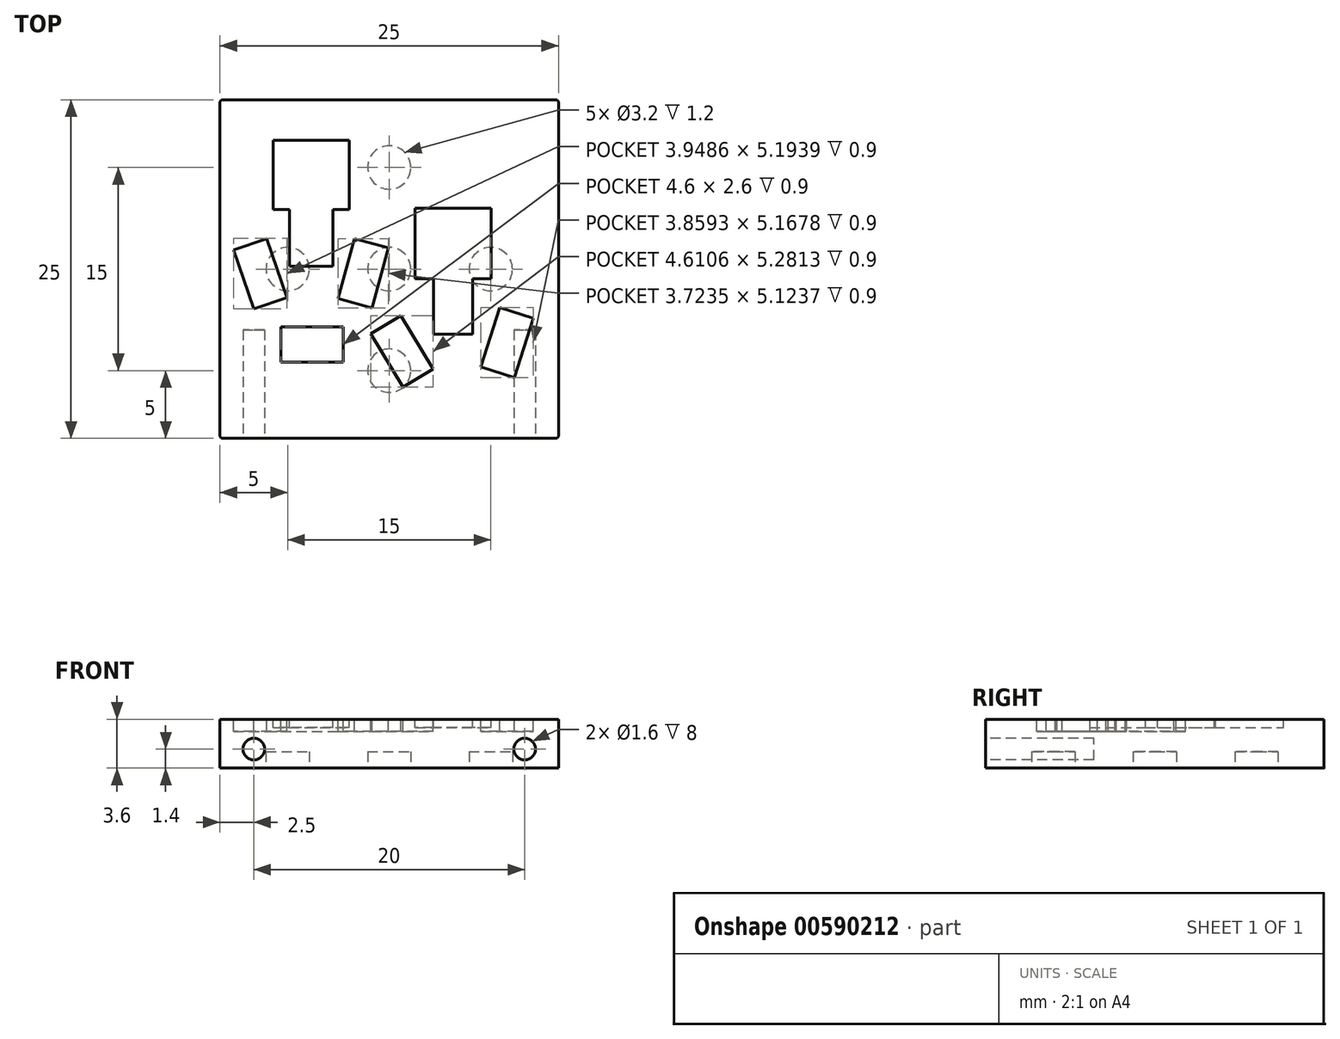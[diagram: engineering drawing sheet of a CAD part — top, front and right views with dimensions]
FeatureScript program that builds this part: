
annotation { "Feature Type Name" : "Feature", "Feature Type Description" : "" }
export const myFeature = defineFeature(function(context is Context, id is Id, definition is map)
    precondition{}
    {
        {
            var Q0;
            Q0=qCreatedBy(makeId("Top.planeOp"),FACE);
            var sketch = newSketch(context, id + "F0", { "sketchPlane" : qUnion([Q0])});
            skLineSegment(sketch, "E0.bottom", {"start": v(-12.5, 12.5) * mm, "end": v(12.5, 12.5) * mm});
            skLineSegment(sketch, "E0.top", {"start": v(-12.5, -12.5) * mm, "end": v(12.5, -12.5) * mm});
            skLineSegment(sketch, "E0.left", {"start": v(-12.5, 12.5) * mm, "end": v(-12.5, -12.5) * mm});
            skLineSegment(sketch, "E0.right", {"start": v(12.5, 12.5) * mm, "end": v(12.5, -12.5) * mm});
            skPoint(sketch, "E0.middle", {"position": v(0, 0) * mm});
            skSolve(sketch);
        }
        {
            var Q0;
            Q0 = qSketchRegion(id + "F0", true);
            extrude(context, id + "F1", {"entities" : qUnion([Q0]), "depth" : 3.6 * mm, "offsetDistance" : 25 * mm});
        }
        {
            var Q0;
            Q0=makeQuery(id+"F1.opExtrude","CAP_FACE",FACE,{"disambiguationData":[OSD([sQuery(id+"F0.wireOp",EDGE,"E0.bottom"),sQuery(id+"F0.wireOp",EDGE,"E0.top"),sQuery(id+"F0.wireOp",EDGE,"E0.left"),sQuery(id+"F0.wireOp",EDGE,"E0.right")])],"isStart":false});
            var sketch = newSketch(context, id + "F2", { "sketchPlane" : qUnion([Q0])});
            skLineSegment(sketch, "E1", {"start": v(-8.57, 9.5) * mm, "end": v(-2.97, 9.5) * mm});
            skLineSegment(sketch, "E2", {"start": v(-2.97, 9.5) * mm, "end": v(-2.97, 4.4) * mm});
            skLineSegment(sketch, "E3", {"start": v(-2.97, 4.4) * mm, "end": v(-4.17, 4.4) * mm});
            skLineSegment(sketch, "E4", {"start": v(-4.17, 4.4) * mm, "end": v(-4.17, 0.2) * mm});
            skLineSegment(sketch, "E5", {"start": v(-4.17, 0.2) * mm, "end": v(-7.37, 0.2) * mm});
            skLineSegment(sketch, "E6", {"start": v(-7.37, 0.2) * mm, "end": v(-7.37, 4.4) * mm});
            skLineSegment(sketch, "E7", {"start": v(-7.37, 4.4) * mm, "end": v(-8.57, 4.4) * mm});
            skLineSegment(sketch, "E8", {"start": v(-8.57, 4.4) * mm, "end": v(-8.57, 9.5) * mm});
            skLineSegment(sketch, "E9", {"start": v(1.91, 4.5) * mm, "end": v(7.51, 4.5) * mm});
            skLineSegment(sketch, "E10", {"start": v(7.51, 4.5) * mm, "end": v(7.51, -0.7) * mm});
            skLineSegment(sketch, "E11", {"start": v(7.51, -0.7) * mm, "end": v(6.16, -0.7) * mm});
            skLineSegment(sketch, "E12", {"start": v(6.16, -0.7) * mm, "end": v(6.16, -4.8) * mm});
            skLineSegment(sketch, "E13", {"start": v(6.16, -4.8) * mm, "end": v(3.26, -4.8) * mm});
            skLineSegment(sketch, "E14", {"start": v(3.26, -4.8) * mm, "end": v(3.26, -0.7) * mm});
            skLineSegment(sketch, "E15", {"start": v(3.26, -0.7) * mm, "end": v(1.91, -0.7) * mm});
            skLineSegment(sketch, "E16", {"start": v(1.91, -0.7) * mm, "end": v(1.91, 4.5) * mm});
            skSolve(sketch);
        }
        {
            var Q0;
            Q0 = qSketchRegion(id + "F2", true);
            extrude(context, id + "F3", {"entities" : qUnion([Q0]), "operationType" : NewBodyOperationType.REMOVE, "oppositeDirection" : true, "depth" : .6 * mm, "offsetDistance" : 25 * mm});
        }
        {
            var Q0;
            Q0=makeQuery(id+"F1.opExtrude","CAP_FACE",FACE,{"disambiguationData":[OSD([sQuery(id+"F0.wireOp",EDGE,"E0.bottom"),sQuery(id+"F0.wireOp",EDGE,"E0.top"),sQuery(id+"F0.wireOp",EDGE,"E0.left"),sQuery(id+"F0.wireOp",EDGE,"E0.right")])],"isStart":false});
            var sketch = newSketch(context, id + "F4", { "sketchPlane" : qUnion([Q0])});
            skLineSegment(sketch, "E17", {"start": v(-9.04, 2.25) * mm, "end": v(-7.55, -2.1) * mm});
            skLineSegment(sketch, "E18", {"start": v(-7.55, -2.1) * mm, "end": v(-10.01, -2.94) * mm});
            skLineSegment(sketch, "E19", {"start": v(-10.01, -2.94) * mm, "end": v(-11.5, 1.41) * mm});
            skLineSegment(sketch, "E20", {"start": v(-11.5, 1.41) * mm, "end": v(-9.04, 2.25) * mm});
            skLineSegment(sketch, "E21", {"start": v(-2.57, 2.25) * mm, "end": v(-3.78, -2.18) * mm});
            skLineSegment(sketch, "E22", {"start": v(-3.78, -2.18) * mm, "end": v(-1.27, -2.87) * mm});
            skLineSegment(sketch, "E23", {"start": v(-1.27, -2.87) * mm, "end": v(-0.06, 1.57) * mm});
            skLineSegment(sketch, "E24", {"start": v(-0.06, 1.57) * mm, "end": v(-2.57, 2.25) * mm});
            skLineSegment(sketch, "E25", {"start": v(-1.37, -4.79) * mm, "end": v(1.02, -8.72) * mm});
            skLineSegment(sketch, "E26", {"start": v(1.02, -8.72) * mm, "end": v(3.24, -7.37) * mm});
            skLineSegment(sketch, "E27", {"start": v(3.24, -7.37) * mm, "end": v(0.86, -3.44) * mm});
            skLineSegment(sketch, "E28", {"start": v(0.86, -3.44) * mm, "end": v(-1.37, -4.79) * mm});
            skLineSegment(sketch, "E29", {"start": v(8.14, -2.84) * mm, "end": v(6.77, -7.23) * mm});
            skLineSegment(sketch, "E30", {"start": v(6.77, -7.23) * mm, "end": v(9.25, -8.01) * mm});
            skLineSegment(sketch, "E31", {"start": v(9.25, -8.01) * mm, "end": v(10.62, -3.62) * mm});
            skLineSegment(sketch, "E32", {"start": v(10.62, -3.62) * mm, "end": v(8.14, -2.84) * mm});
            skLineSegment(sketch, "E33", {"start": v(-8, -4.26) * mm, "end": v(-3.4, -4.26) * mm});
            skLineSegment(sketch, "E34", {"start": v(-3.4, -4.26) * mm, "end": v(-3.4, -6.86) * mm});
            skLineSegment(sketch, "E35", {"start": v(-3.4, -6.86) * mm, "end": v(-8, -6.86) * mm});
            skLineSegment(sketch, "E36", {"start": v(-8, -6.86) * mm, "end": v(-8, -4.26) * mm});
            skSolve(sketch);
        }
        {
            var Q0;
            Q0 = qSketchRegion(id + "F4", true);
            extrude(context, id + "F5", {"entities" : qUnion([Q0]), "operationType" : NewBodyOperationType.REMOVE, "oppositeDirection" : true, "depth" : .9 * mm, "offsetDistance" : 25 * mm});
        }
        {
            var Q0;
            Q0=makeQuery(id+"F1.opExtrude","CAP_FACE",FACE,{"disambiguationData":[OSD([sQuery(id+"F0.wireOp",EDGE,"E0.bottom"),sQuery(id+"F0.wireOp",EDGE,"E0.top"),sQuery(id+"F0.wireOp",EDGE,"E0.left"),sQuery(id+"F0.wireOp",EDGE,"E0.right")])],"isStart":true});
            var sketch = newSketch(context, id + "F6", { "sketchPlane" : qUnion([Q0])});
            skCircle(sketch, "E37", {"center": v(0, 7.5) * mm, "radius": 1.6 * mm});
            skCircle(sketch, "E38", {"center": v(0, 0) * mm, "radius": 1.6 * mm});
            skCircle(sketch, "E39", {"center": v(0, -7.5) * mm, "radius": 1.6 * mm});
            skCircle(sketch, "E40", {"center": v(-7.5, 0) * mm, "radius": 1.6 * mm});
            skCircle(sketch, "E41", {"center": v(7.5, 0) * mm, "radius": 1.6 * mm});
            skSolve(sketch);
        }
        {
            var Q0;
            Q0 = qSketchRegion(id + "F6", true);
            extrude(context, id + "F7", {"entities" : qUnion([Q0]), "operationType" : NewBodyOperationType.REMOVE, "oppositeDirection" : true, "depth" : 1.2 * mm, "offsetDistance" : 25 * mm});
        }
        {
            var Q0;
            Q0=makeQuery(id+"F1.opExtrude","SWEPT_EDGE",EDGE,{"disambiguationData":[OSD([sQuery(id+"F0.wireOp",EDGE,"E0.top"),sQuery(id+"F0.wireOp",EDGE,"E0.left")])]});
            var Q1;
            Q1=makeQuery(id+"F1.opExtrude","SWEPT_EDGE",EDGE,{"disambiguationData":[OSD([sQuery(id+"F0.wireOp",EDGE,"E0.top"),sQuery(id+"F0.wireOp",EDGE,"E0.right")])]});
            var Q2;
            Q2=makeQuery(id+"F1.opExtrude","SWEPT_EDGE",EDGE,{"disambiguationData":[OSD([sQuery(id+"F0.wireOp",EDGE,"E0.bottom"),sQuery(id+"F0.wireOp",EDGE,"E0.right")])]});
            var Q3;
            Q3=makeQuery(id+"F1.opExtrude","SWEPT_EDGE",EDGE,{"disambiguationData":[OSD([sQuery(id+"F0.wireOp",EDGE,"E0.bottom"),sQuery(id+"F0.wireOp",EDGE,"E0.left")])]});
            fillet(context, id + "F8", {"entities" : qUnion([Q0, Q1, Q2, Q3]), "radius" : .2 * mm, "tangentPropagation" : true, "allowEdgeOverflow" : false});
        }
        {
            var Q0;
            Q0=makeQuery(id+"F1.opExtrude","SWEPT_FACE",FACE,{"disambiguationData":[OSD([sQuery(id+"F0.wireOp",EDGE,"E0.top")])]});
            var sketch = newSketch(context, id + "F9", { "sketchPlane" : qUnion([Q0])});
            skCircle(sketch, "E42", {"center": v(-10, 1.4) * mm, "radius": 0.8 * mm});
            skCircle(sketch, "E43", {"center": v(10, 1.4) * mm, "radius": 0.8 * mm});
            skSolve(sketch);
        }
        {
            var Q0;
            Q0 = qSketchRegion(id + "F9", true);
            extrude(context, id + "F10", {"entities" : qUnion([Q0]), "operationType" : NewBodyOperationType.REMOVE, "oppositeDirection" : true, "depth" : 8 * mm, "offsetDistance" : 25 * mm});
        }
    });
